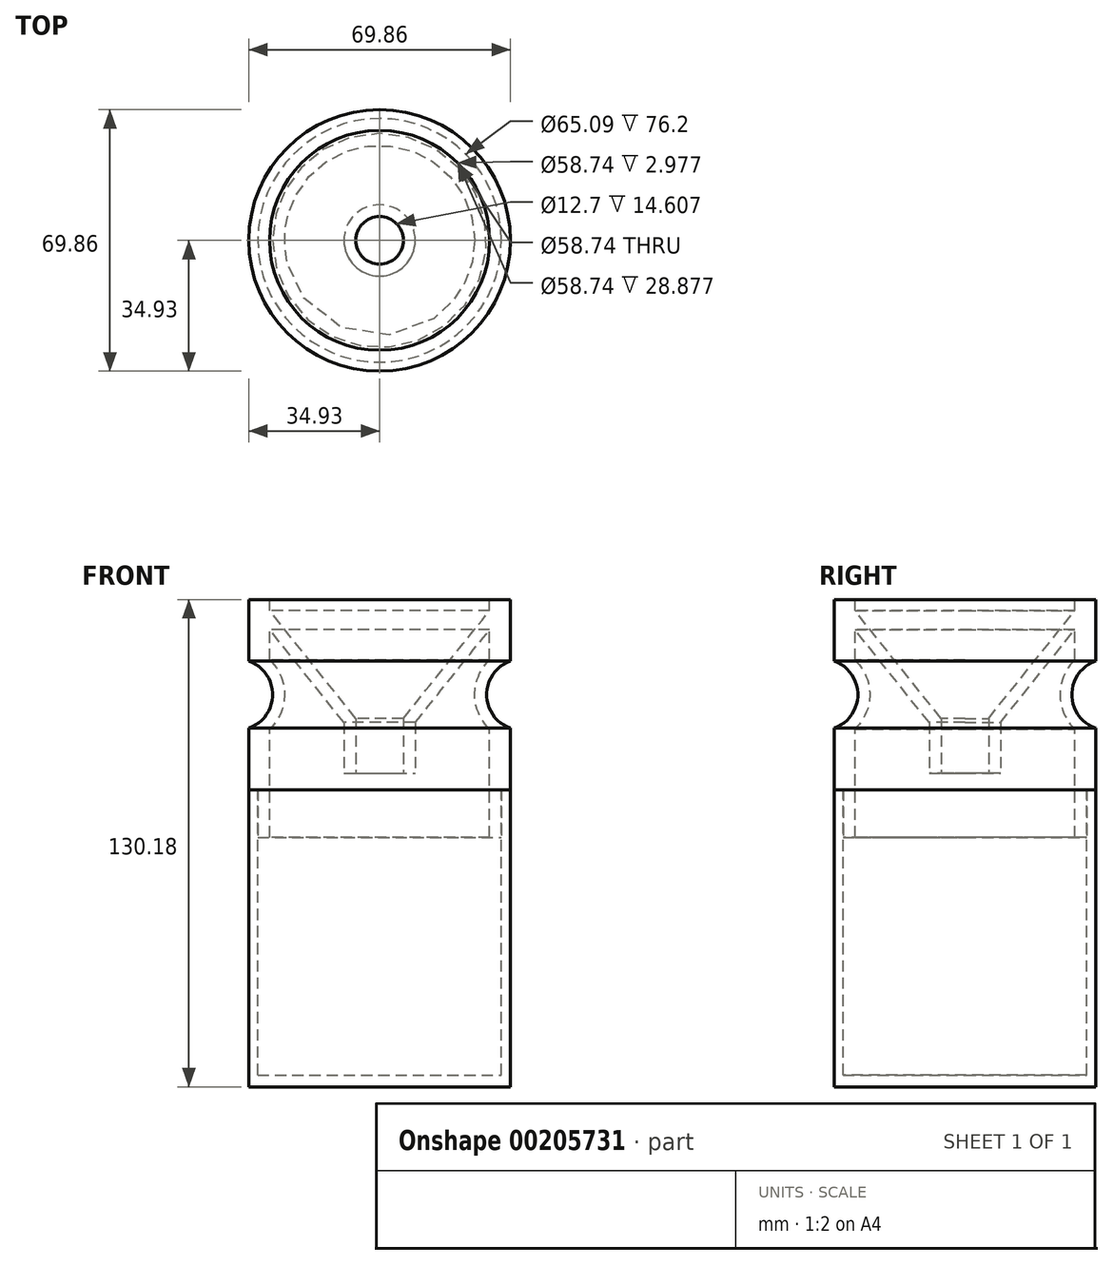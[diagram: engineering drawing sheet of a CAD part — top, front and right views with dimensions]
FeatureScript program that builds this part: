
annotation { "Feature Type Name" : "Feature", "Feature Type Description" : "" }
export const myFeature = defineFeature(function(context is Context, id is Id, definition is map)
    precondition{}
    {
        {
            var Q0;
            Q0=qCreatedBy(makeId("Top.planeOp"),FACE);
            var sketch = newSketch(context, id + "F0", { "sketchPlane" : qUnion([Q0])});
            skCircle(sketch, "E0", {"center": v(0, 0) * mm, "radius": 34.93 * mm});
            skSolve(sketch);
        }
        {
            var Q0;
            Q0 = qSketchRegion(id + "F0", true);
            extrude(context, id + "F1", {"entities" : qUnion([Q0]), "depth" : 127 * mm});
        }
        {
            var Q0;
            Q0=makeQuery(id+"F1.opExtrude","CAP_FACE",FACE,{"disambiguationData":[OSD([sQuery(id+"F0.wireOp",EDGE,"E0")])],"isStart":false});
            var sketch = newSketch(context, id + "F2", { "sketchPlane" : qUnion([Q0])});
            skCircle(sketch, "E1", {"center": v(0, 0) * mm, "radius": 29.37 * mm});
            skSolve(sketch);
        }
        {
            var Q0;
            Q0 = qSketchRegion(id + "F2", true);
            extrude(context, id + "F3", {"entities" : qUnion([Q0]), "operationType" : NewBodyOperationType.REMOVE, "oppositeDirection" : true, "depth" : 120.65 * mm});
        }
        {
            var Q0;
            Q0=qCreatedBy(makeId("Right.planeOp"),FACE);
            var sketch = newSketch(context, id + "F4", { "sketchPlane" : qUnion([Q0])});
            skLineSegment(sketch, "E2", {"start": v(0, 0) * mm, "end": v(0, 95.25) * mm});
            skLineSegment(sketch, "E3", {"start": v(0, 95.25) * mm, "end": v(6.35, 95.25) * mm, "construction": true});
            skLineSegment(sketch, "E4", {"start": v(6.35, 95.25) * mm, "end": v(31.75, 127) * mm});
            skLineSegment(sketch, "E5", {"start": v(31.75, 127) * mm, "end": v(31.75, 121.92) * mm});
            skLineSegment(sketch, "E6", {"start": v(31.75, 121.92) * mm, "end": v(6.35, 90.17) * mm});
            skLineSegment(sketch, "E7", {"start": v(6.35, 95.25) * mm, "end": v(6.35, 90.17) * mm});
            skLineSegment(sketch, "E8", {"start": v(6.35, 90.17) * mm, "end": v(6.35, 80.64) * mm});
            skLineSegment(sketch, "E9", {"start": v(6.35, 80.64) * mm, "end": v(9.52, 80.64) * mm});
            skLineSegment(sketch, "E10", {"start": v(9.53, 80.64) * mm, "end": v(9.53, 94.14) * mm});
            skSolve(sketch);
        }
        {
            var Q0;
            Q0=qCreatedBy(makeId("Right.planeOp"),FACE);
            var sketch = newSketch(context, id + "F5", { "sketchPlane" : qUnion([Q0])});
            skLineSegment(sketch, "E11", {"start": v(0, 0) * mm, "end": v(0, 142.78) * mm, "construction": true});
            skSolve(sketch);
        }
        {
            var Q0;
            Q0=makeQuery(id+"F4.imprint","IMPRINT",FACE,{"disambiguationData":[TD([[makeQuery(id+"F4.imprint","IMPRINT",EDGE,{"derivedFrom":sQuery(id+"F4.wireOp",EDGE,"E4")}),-1.0]])]});
            var Q1;
            {var subQ0=sQuery(id+"F4.wireOp",EDGE,"E8");Q1=makeQuery(id+"F4.imprint","IMPRINT",FACE,{"disambiguationData":[TD([[makeQuery(id+"F4.imprint","IMPRINT",EDGE,{"derivedFrom":subQ0}),1.0]])]});}
            var Q2;
            Q2=sQuery(id+"F5.wireOp",EDGE,"E11");
            revolve(context, id + "F6", {"operationType" : NewBodyOperationType.ADD, "entities" : qUnion([Q0, Q1]), "axis" : qUnion([Q2]), "revolveType" : RevolveType.FULL});
        }
        {
            var Q0;
            Q0=qCreatedBy(makeId("Top.planeOp"),FACE);
            cPlane(context, id + "F7", {"entities" : qUnion([Q0]), "cplaneType" : CPlaneType.OFFSET, "offset" : 123.82 * mm, "width" : 152.4 * mm, "height" : 152.4 * mm});
        }
        {
            var Q0;
            Q0=makeQuery(id+"F1.opExtrude","CAP_EDGE",EDGE,{"disambiguationData":[OSD([sQuery(id+"F0.wireOp",EDGE,"E0")])],"isStart":true});
            fillet(context, id + "F8", {"entities" : qUnion([Q0]), "radius" : 3.17 * mm, "tangentPropagation" : true, "allowEdgeOverflow" : false});
        }
        {
            var Q0;
            Q0=qCreatedBy(makeId("Right.planeOp"),FACE);
            var sketch = newSketch(context, id + "F9", { "sketchPlane" : qUnion([Q0])});
            skLineSegment(sketch, "E12", {"start": v(0, 0) * mm, "end": v(0, 127) * mm});
            skLineSegment(sketch, "E13", {"start": v(0, 127) * mm, "end": v(34.93, 127) * mm});
            skLineSegment(sketch, "E14", {"start": v(34.93, 127) * mm, "end": v(34.93, 101.6) * mm});
            skLineSegment(sketch, "E15", {"start": v(38.1, 101.6) * mm, "end": v(34.93, 101.6) * mm});
            skLineSegment(sketch, "E16", {"start": v(34.93, 101.6) * mm, "end": v(34.93, 101.6) * mm});
            skCircle(sketch, "E17", {"center": v(38.1, 101.6) * mm, "radius": 9.53 * mm});
            skCircle(sketch, "E18", {"center": v(38.1, 101.6) * mm, "radius": 12.7 * mm});
            skLineSegment(sketch, "E19", {"start": v(34.93, 101.6) * mm, "end": v(34.93, 89.3) * mm});
            skSolve(sketch);
        }
        {
            var Q0;
            {var subQ0=sQuery(id+"F9.wireOp",EDGE,"E18");var subQ1=sQuery(id+"F9.wireOp",EDGE,"E14");var subQ2=makeQuery(id+"F9.imprint","INTERSECT",VERTEX,{"derivedFrom":[subQ1,subQ0]});Q0=makeQuery(id+"F9.imprint","IMPRINT",FACE,{"disambiguationData":[TD([[makeQuery(id+"F9.imprint","IMPRINT",EDGE,{"disambiguationData":[TD([[subQ2,-1.0]])],"derivedFrom":subQ1}),-1.0]])]});}
            var Q1;
            Q1=sQuery(id+"F9.wireOp",EDGE,"E12");
            revolve(context, id + "F10", {"operationType" : NewBodyOperationType.ADD, "entities" : qUnion([Q0]), "axis" : qUnion([Q1]), "revolveType" : RevolveType.FULL});
        }
        {
            var Q0;
            Q0=qCreatedBy(makeId("Right.planeOp"),FACE);
            var sketch = newSketch(context, id + "F11", { "sketchPlane" : qUnion([Q0])});
            skLineSegment(sketch, "E20", {"start": v(0, 0) * mm, "end": v(0, 127) * mm});
            skLineSegment(sketch, "E21", {"start": v(0, 127) * mm, "end": v(38.1, 127) * mm});
            skLineSegment(sketch, "E22", {"start": v(38.1, 127) * mm, "end": v(38.1, 101.6) * mm});
            skCircle(sketch, "E23", {"center": v(38.1, 101.6) * mm, "radius": 9.53 * mm});
            skSolve(sketch);
        }
        {
            var Q0;
            Q0 = qSketchRegion(id + "F11", true);
            var Q1;
            Q1=sQuery(id+"F11.wireOp",EDGE,"E20");
            revolve(context, id + "F12", {"operationType" : NewBodyOperationType.REMOVE, "entities" : qUnion([Q0]), "axis" : qUnion([Q1]), "revolveType" : RevolveType.FULL, "oppositeDirection" : true});
        }
        {
            var Q0;
            Q0=qCreatedBy(makeId("Top.planeOp"),FACE);
            var sketch = newSketch(context, id + "F13", { "sketchPlane" : qUnion([Q0])});
            skCircle(sketch, "E24", {"center": v(0, 0) * mm, "radius": 34.93 * mm});
            skSolve(sketch);
        }
        {
            var Q0;
            Q0 = qSketchRegion(id + "F13", true);
            extrude(context, id + "F14", {"entities" : qUnion([Q0]), "operationType" : NewBodyOperationType.REMOVE, "depth" : 63.5 * mm});
        }
        {
            var Q0;
            Q0=makeQuery(id+"F14.boolean.opBoolean","COPY",FACE,{"derivedFrom":makeQuery(id+"F14.opExtrude","CAP_FACE",FACE,{"disambiguationData":[OSD([sQuery(id+"F13.wireOp",EDGE,"E24")])],"isStart":false})});
            var sketch = newSketch(context, id + "F15", { "sketchPlane" : qUnion([Q0])});
            skCircle(sketch, "E25", {"center": v(0, 0) * mm, "radius": 32.54 * mm});
            skCircle(sketch, "E26", {"center": v(0, 0) * mm, "radius": 34.93 * mm});
            skSolve(sketch);
        }
        {
            var Q0;
            Q0 = qSketchRegion(id + "F15", true);
            extrude(context, id + "F16", {"entities" : qUnion([Q0]), "operationType" : NewBodyOperationType.REMOVE, "oppositeDirection" : true, "depth" : 12.7 * mm});
        }
        {
            var Q0;
            Q0=makeQuery(id+"F16.boolean.opBoolean","COPY",FACE,{"derivedFrom":makeQuery(id+"F16.opExtrude","CAP_FACE",FACE,{"disambiguationData":[OSD([sQuery(id+"F15.wireOp",EDGE,"E25"),sQuery(id+"F15.wireOp",EDGE,"E26")])],"isStart":false})});
            var sketch = newSketch(context, id + "F17", { "sketchPlane" : qUnion([Q0])});
            skCircle(sketch, "E27", {"center": v(0, 0) * mm, "radius": 32.54 * mm});
            skCircle(sketch, "E28", {"center": v(0, 0) * mm, "radius": 34.93 * mm});
            skSolve(sketch);
        }
        {
            var Q0;
            Q0 = qSketchRegion(id + "F17", true);
            extrude(context, id + "F18", {"entities" : qUnion([Q0]), "depth" : 76.2 * mm});
        }
        {
            var Q0;
            Q0=makeQuery(id+"F18.opExtrude","CAP_FACE",FACE,{"disambiguationData":[OSD([sQuery(id+"F17.wireOp",EDGE,"E27"),sQuery(id+"F17.wireOp",EDGE,"E28")])],"isStart":false});
            var sketch = newSketch(context, id + "F19", { "sketchPlane" : qUnion([Q0])});
            skCircle(sketch, "E29", {"center": v(0, 0) * mm, "radius": 34.93 * mm});
            skSolve(sketch);
        }
        {
            var Q0;
            Q0 = qSketchRegion(id + "F19", true);
            extrude(context, id + "F20", {"entities" : qUnion([Q0]), "operationType" : NewBodyOperationType.ADD, "depth" : 3.17 * mm});
        }
    });
